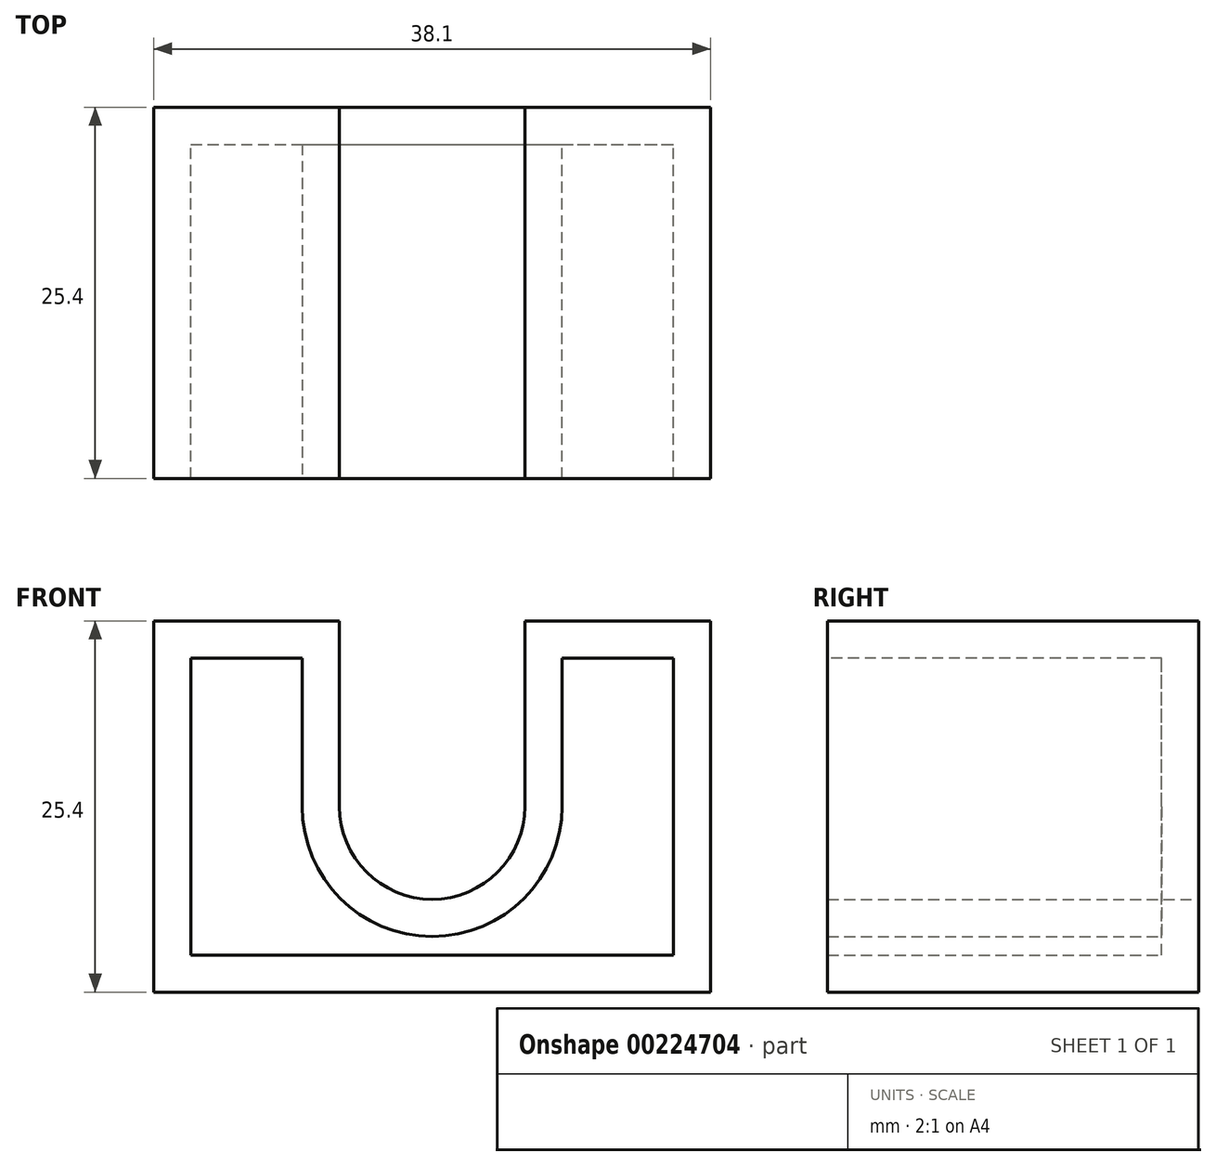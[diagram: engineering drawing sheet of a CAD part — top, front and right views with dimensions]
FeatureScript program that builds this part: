
annotation { "Feature Type Name" : "Feature", "Feature Type Description" : "" }
export const myFeature = defineFeature(function(context is Context, id is Id, definition is map)
    precondition{}
    {
        {
            var Q0;
            Q0=qCreatedBy(makeId("Front.planeOp"),FACE);
            var sketch = newSketch(context, id + "F0", { "sketchPlane" : qUnion([Q0])});
            skLineSegment(sketch, "E0.bottom", {"start": v(0, 0) * mm, "end": v(38.1, 0) * mm});
            skLineSegment(sketch, "E0.left", {"start": v(0, 0) * mm, "end": v(0, 25.4) * mm});
            skLineSegment(sketch, "E1", {"start": v(38.1, 0) * mm, "end": v(38.1, 25.4) * mm});
            skLineSegment(sketch, "E2", {"start": v(0, 25.4) * mm, "end": v(38.1, 25.4) * mm});
            skCircle(sketch, "E3", {"center": v(19.05, 12.7) * mm, "radius": 6.35 * mm});
            skSolve(sketch);
        }
        {
            var Q0;
            Q0=makeQuery(id+"F0.imprint","IMPRINT",FACE,{"disambiguationData":[TD([[makeQuery(id+"F0.imprint","IMPRINT",EDGE,{"derivedFrom":sQuery(id+"F0.wireOp",EDGE,"E0.bottom")}),1.0]])]});
            extrude(context, id + "F1", {"entities" : qUnion([Q0]), "depth" : 25.4 * mm});
        }
        {
            var Q0;
            Q0=makeQuery(id+"F1.opExtrude","SWEPT_FACE",FACE,{"disambiguationData":[OSD([sQuery(id+"F0.wireOp",EDGE,"E2")])]});
            var sketch = newSketch(context, id + "F2", { "sketchPlane" : qUnion([Q0])});
            skLineSegment(sketch, "E4", {"start": v(12.7, 0) * mm, "end": v(12.7, -25.4) * mm});
            skLineSegment(sketch, "E5", {"start": v(25.4, -25.4) * mm, "end": v(25.4, 0) * mm});
            skLineSegment(sketch, "E6", {"start": v(12.7, 0) * mm, "end": v(25.4, 0) * mm});
            skLineSegment(sketch, "E7", {"start": v(12.7, -25.4) * mm, "end": v(25.4, -25.4) * mm});
            skSolve(sketch);
        }
        {
            var Q0;
            Q0=makeQuery(id+"F2.imprint","IMPRINT",FACE,{"disambiguationData":[TD([[makeQuery(id+"F2.imprint","IMPRINT",EDGE,{"derivedFrom":sQuery(id+"F2.wireOp",EDGE,"E4")}),1.0]])]});
            extrude(context, id + "F3", {"entities" : qUnion([Q0]), "operationType" : NewBodyOperationType.REMOVE, "oppositeDirection" : true, "depth" : 12.7 * mm});
        }
        {
            var Q0;
            Q0=makeQuery(id+"F1.opExtrude","CAP_FACE",FACE,{"disambiguationData":[OSD([sQuery(id+"F0.wireOp",EDGE,"E0.bottom"),sQuery(id+"F0.wireOp",EDGE,"E0.left"),sQuery(id+"F0.wireOp",EDGE,"E1"),sQuery(id+"F0.wireOp",EDGE,"E2"),sQuery(id+"F0.wireOp",EDGE,"E3")])],"isStart":false});
            shell(context, id + "F4", {"entities" : qUnion([Q0]), "thickness" : 2.54 * mm});
        }
    });
